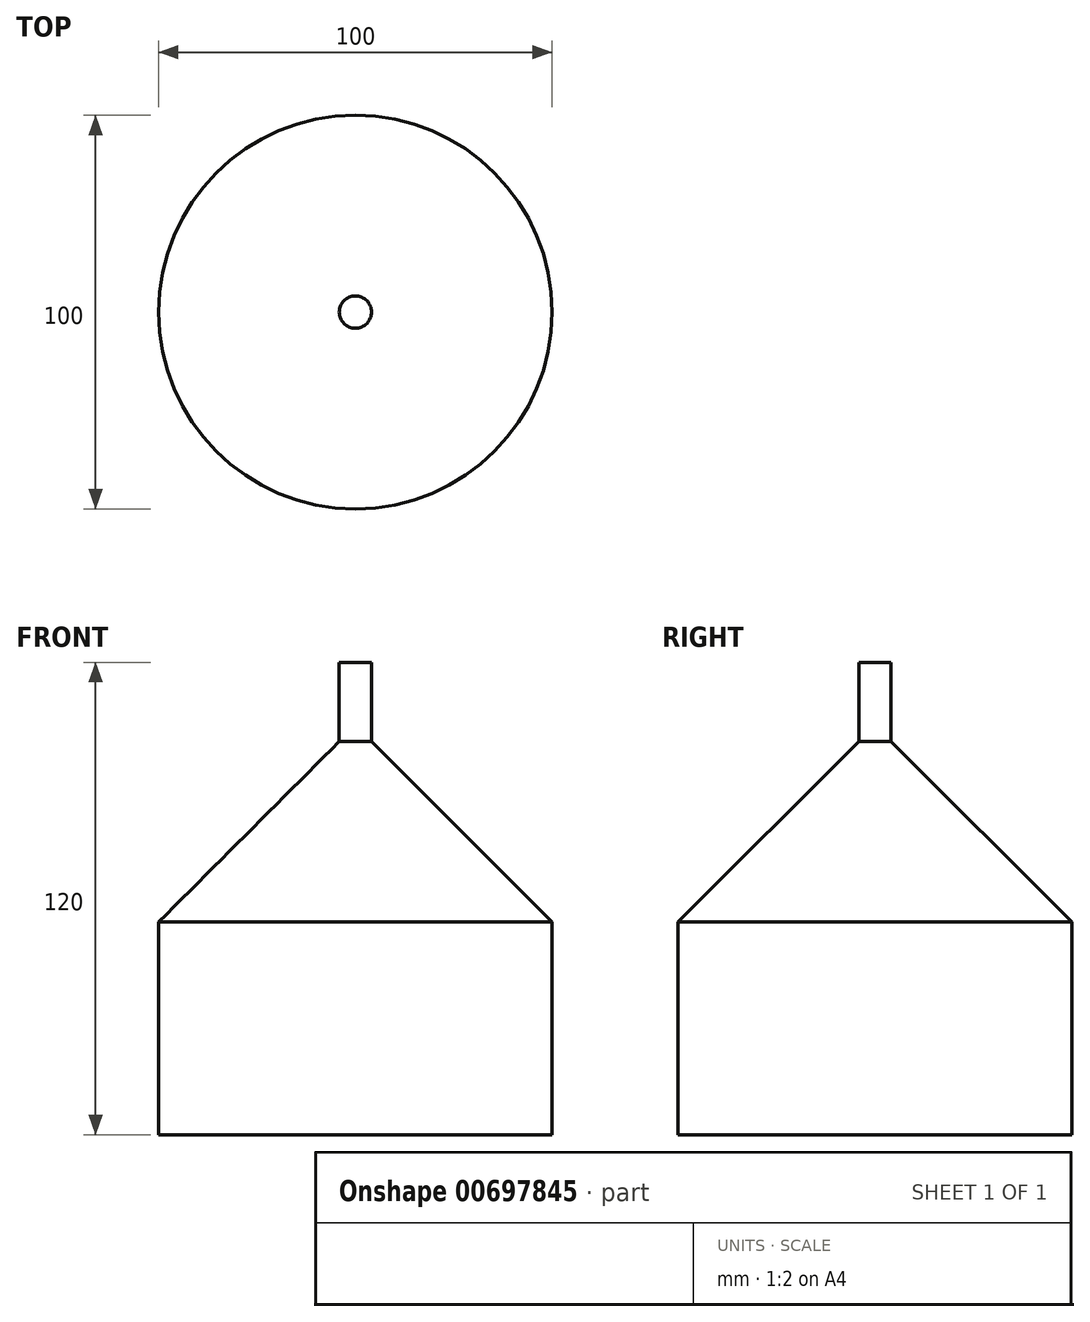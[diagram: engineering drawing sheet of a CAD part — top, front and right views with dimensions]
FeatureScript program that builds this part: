
annotation { "Feature Type Name" : "Feature", "Feature Type Description" : "" }
export const myFeature = defineFeature(function(context is Context, id is Id, definition is map)
    precondition{}
    {
        {
            var Q0;
            Q0=qCreatedBy(makeId("Top.planeOp"),FACE);
            var sketch = newSketch(context, id + "F0", { "sketchPlane" : qUnion([Q0])});
            skCircle(sketch, "E0", {"center": v(0, 0) * mm, "radius": 50 * mm});
            skSolve(sketch);
        }
        {
            var Q0;
            Q0 = qSketchRegion(id + "F0", true);
            extrude(context, id + "F1", {"entities" : qUnion([Q0]), "depth" : 100 * mm, "offsetDistance" : 25 * mm});
        }
        {
            var Q0;
            Q0=makeQuery(id+"F1.opExtrude","CAP_FACE",FACE,{"disambiguationData":[OSD([sQuery(id+"F0.wireOp",EDGE,"E0")])],"isStart":false});
            var sketch = newSketch(context, id + "F2", { "sketchPlane" : qUnion([Q0])});
            skCircle(sketch, "E1", {"center": v(0, 0) * mm, "radius": 4.1 * mm});
            skSolve(sketch);
        }
        {
            var Q0;
            Q0=makeQuery(id+"F2.imprint","IMPRINT",FACE,{"disambiguationData":[TD([[makeQuery(id+"F2.imprint","IMPRINT",EDGE,{"derivedFrom":sQuery(id+"F2.wireOp",EDGE,"E1")}),1.0]])]});
            var Q1;
            Q1=sQuery(id+"F2.wireOp",EDGE,"E1");
            extrude(context, id + "F3", {"entities" : qUnion([Q0]), "operationType" : NewBodyOperationType.ADD, "surfaceOperationType" : NewSurfaceOperationType.ADD, "surfaceEntities" : qUnion([Q1]), "depth" : 20 * mm, "offsetDistance" : 25 * mm});
        }
        {
            var Q0;
            Q0=makeQuery(id+"F1.opExtrude","CAP_EDGE",EDGE,{"disambiguationData":[OSD([sQuery(id+"F0.wireOp",EDGE,"E0")])],"isStart":false});
            chamfer(context, id + "F4", {"entities" : qUnion([Q0]), "width" : 46 * mm, "tangentPropagation" : true});
        }
    });
